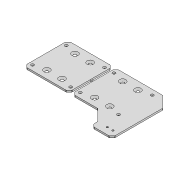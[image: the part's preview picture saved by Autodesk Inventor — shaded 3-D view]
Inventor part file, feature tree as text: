
AUTODESK INVENTOR PART (.ipt)
format: ipt  version: 2020 (Build 240168000, 168)  size: 198,656 bytes
history: native  units: mm
features: other x4, extrude x1, sketch x1, projected_geometry x1
ambient origin geometry x8: Origin, YZ Plane, XZ Plane, XY Plane, X Axis, Y Axis, Z Axis, Center Point
bodies: Body1 (feature_tree)
feature tree (7):
  other  "CCM_Mount_AB.iam"
  other  "CCM_Mount_A.ipt:1"
  other  "CCM_Mount_B.ipt:1"
  other  "ソリッド1"
  extrude  "押し出し1"  Depth=10.0mm
  sketch  "スケッチ1"
  projected_geometry  "投影ループ1"
